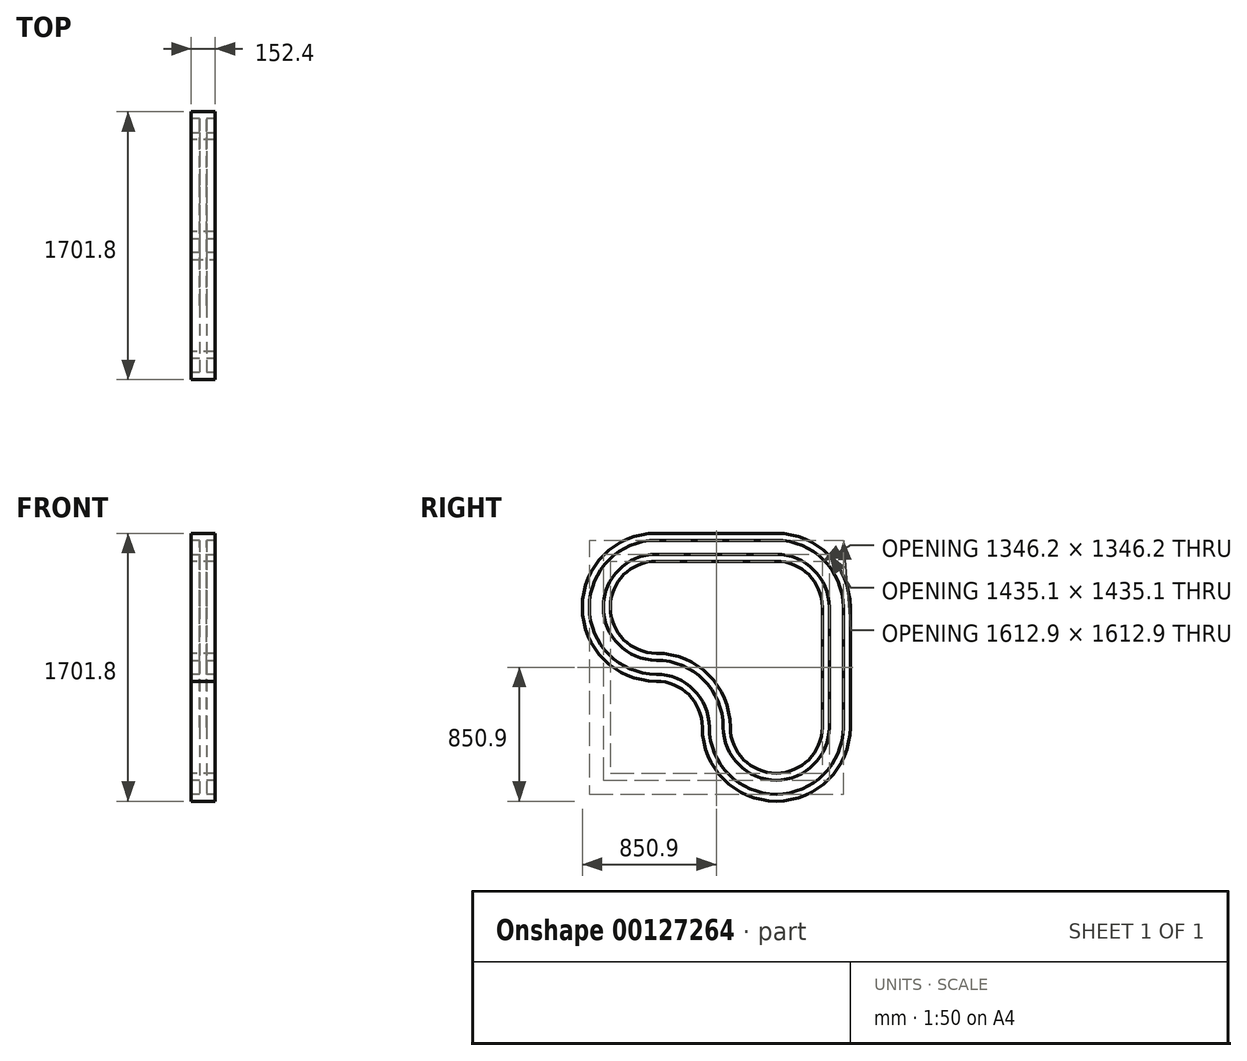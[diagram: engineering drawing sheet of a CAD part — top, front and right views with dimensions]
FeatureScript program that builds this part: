
annotation { "Feature Type Name" : "Feature", "Feature Type Description" : "" }
export const myFeature = defineFeature(function(context is Context, id is Id, definition is map)
    precondition{}
    {
        {
            var Q0;
            Q0=qCreatedBy(makeId("Front.planeOp"),FACE);
            var sketch = newSketch(context, id + "F0", { "sketchPlane" : qUnion([Q0])});
            skLineSegment(sketch, "E0", {"start": v(-76.2, 88.9) * mm, "end": v(-76.2, 44.45) * mm});
            skLineSegment(sketch, "E1", {"start": v(-76.2, 44.45) * mm, "end": v(-22.22, 44.45) * mm});
            skLineSegment(sketch, "E2", {"start": v(-22.23, 44.45) * mm, "end": v(-22.22, -44.45) * mm});
            skLineSegment(sketch, "E3", {"start": v(-22.22, -44.45) * mm, "end": v(-76.2, -44.45) * mm});
            skLineSegment(sketch, "E4", {"start": v(-76.2, -44.45) * mm, "end": v(-76.2, -88.9) * mm});
            skLineSegment(sketch, "E5", {"start": v(-76.2, -88.9) * mm, "end": v(76.2, -88.9) * mm});
            skLineSegment(sketch, "E6", {"start": v(76.2, -88.9) * mm, "end": v(76.2, -44.45) * mm});
            skLineSegment(sketch, "E7", {"start": v(76.2, -44.45) * mm, "end": v(22.22, -44.45) * mm});
            skLineSegment(sketch, "E8", {"start": v(22.22, -44.45) * mm, "end": v(22.22, 44.45) * mm});
            skLineSegment(sketch, "E9", {"start": v(22.22, 44.45) * mm, "end": v(76.2, 44.45) * mm});
            skLineSegment(sketch, "E10", {"start": v(76.2, 44.45) * mm, "end": v(76.2, 88.9) * mm});
            skLineSegment(sketch, "E11", {"start": v(76.2, 88.9) * mm, "end": v(-76.2, 88.9) * mm});
            skLineSegment(sketch, "E12", {"start": v(0, 88.9) * mm, "end": v(0, -88.9) * mm, "construction": true});
            skLineSegment(sketch, "E13", {"start": v(-22.22, 0) * mm, "end": v(22.22, 0) * mm, "construction": true});
            skSolve(sketch);
        }
        {
            var Q0;
            Q0=qCreatedBy(makeId("Right.planeOp"),FACE);
            var sketch = newSketch(context, id + "F1", { "sketchPlane" : qUnion([Q0])});
            skArc(sketch, "E14", {"start": v(381, -381) * mm, "mid": v(269.4, -111.6) * mm, "end": v(0, 0) * mm});
            skArc(sketch, "E15", {"start": v(381, -381) * mm, "mid": v(492.6, -650.4) * mm, "end": v(762, -762) * mm});
            skPoint(sketch, "E15.endSnap0", {"position": v(0, -762) * mm});
            skArc(sketch, "E16", {"start": v(762, -762) * mm, "mid": v(1031.4, -650.4) * mm, "end": v(1143, -381) * mm});
            skLineSegment(sketch, "E17", {"start": v(1143, -381) * mm, "end": v(1143, 381) * mm});
            skLineSegment(sketch, "E18", {"start": v(762, 762) * mm, "end": v(0, 762) * mm});
            skArc(sketch, "E19", {"start": v(0, 762) * mm, "mid": v(-381, 381) * mm, "end": v(0, 0) * mm});
            skPoint(sketch, "E20.visualSharp", {"position": v(1143, 762) * mm});
            skArc(sketch, "E20.filletArc", {"start": v(1143, 381) * mm, "mid": v(1031.4, 650.4) * mm, "end": v(762, 762) * mm});
            skSolve(sketch);
        }
        {
            var Q0;
            Q0=makeQuery(id+"F0.imprint","IMPRINT",FACE,{"disambiguationData":[TD([[makeQuery(id+"F0.imprint","IMPRINT",EDGE,{"derivedFrom":sQuery(id+"F0.wireOp",EDGE,"E0")}),1.0]])]});
            var Q1;
            Q1 = qConstructionFilter(qBodyType(qCreatedBy(id + "F1" ,EDGE), BodyType.WIRE), ConstructionObject.NO);
            sweep(context, id + "F2", {"profiles" : qUnion([Q0]), "path" : qUnion([Q1])});
        }
    });
